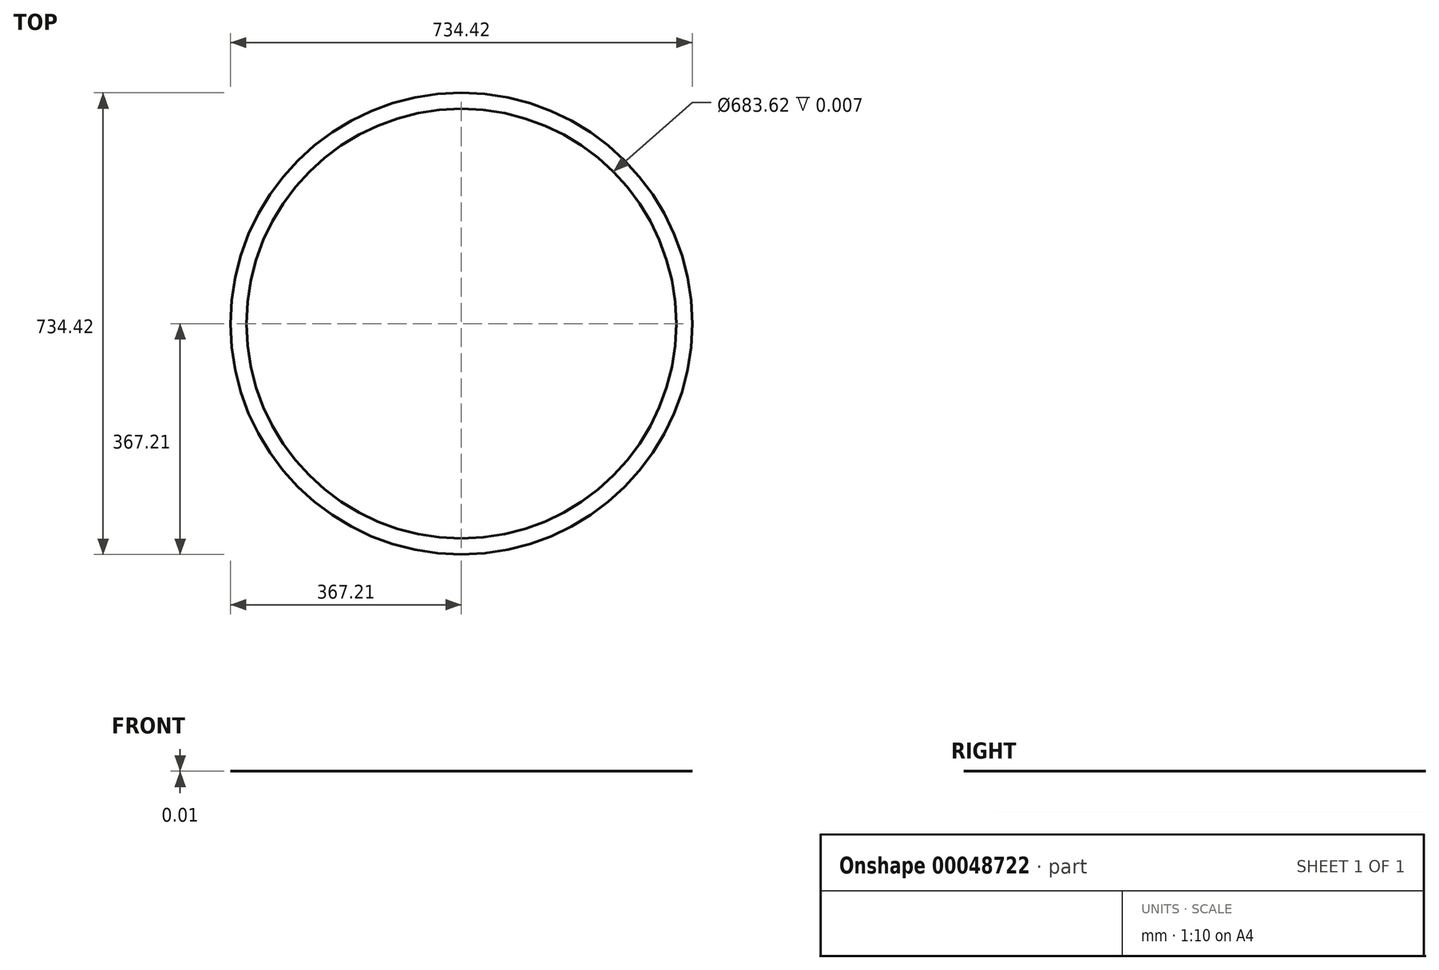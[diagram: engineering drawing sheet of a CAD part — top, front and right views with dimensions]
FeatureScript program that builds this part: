
annotation { "Feature Type Name" : "Feature", "Feature Type Description" : "" }
export const myFeature = defineFeature(function(context is Context, id is Id, definition is map)
    precondition{}
    {
        {
            var Q0;
            Q0=qCreatedBy(makeId("Top.planeOp"),FACE);
            var sketch = newSketch(context, id + "F0", { "sketchPlane" : qUnion([Q0])});
            skCircle(sketch, "E0", {"center": v(0, 0) * mm, "radius": 367.21 * mm});
            skCircle(sketch, "E1", {"center": v(0, 0) * mm, "radius": 341.81 * mm});
            skSolve(sketch);
        }
        {
            var Q0;
            Q0=makeQuery(id+"F0.imprint","IMPRINT",FACE,{"disambiguationData":[TD([[makeQuery(id+"F0.imprint","IMPRINT",EDGE,{"derivedFrom":sQuery(id+"F0.wireOp",EDGE,"E0")}),1.0]])]});
            extrude(context, id + "F1", {"entities" : qUnion([Q0]), "depth" : 3 / 406.4 * mm});
        }
    });
